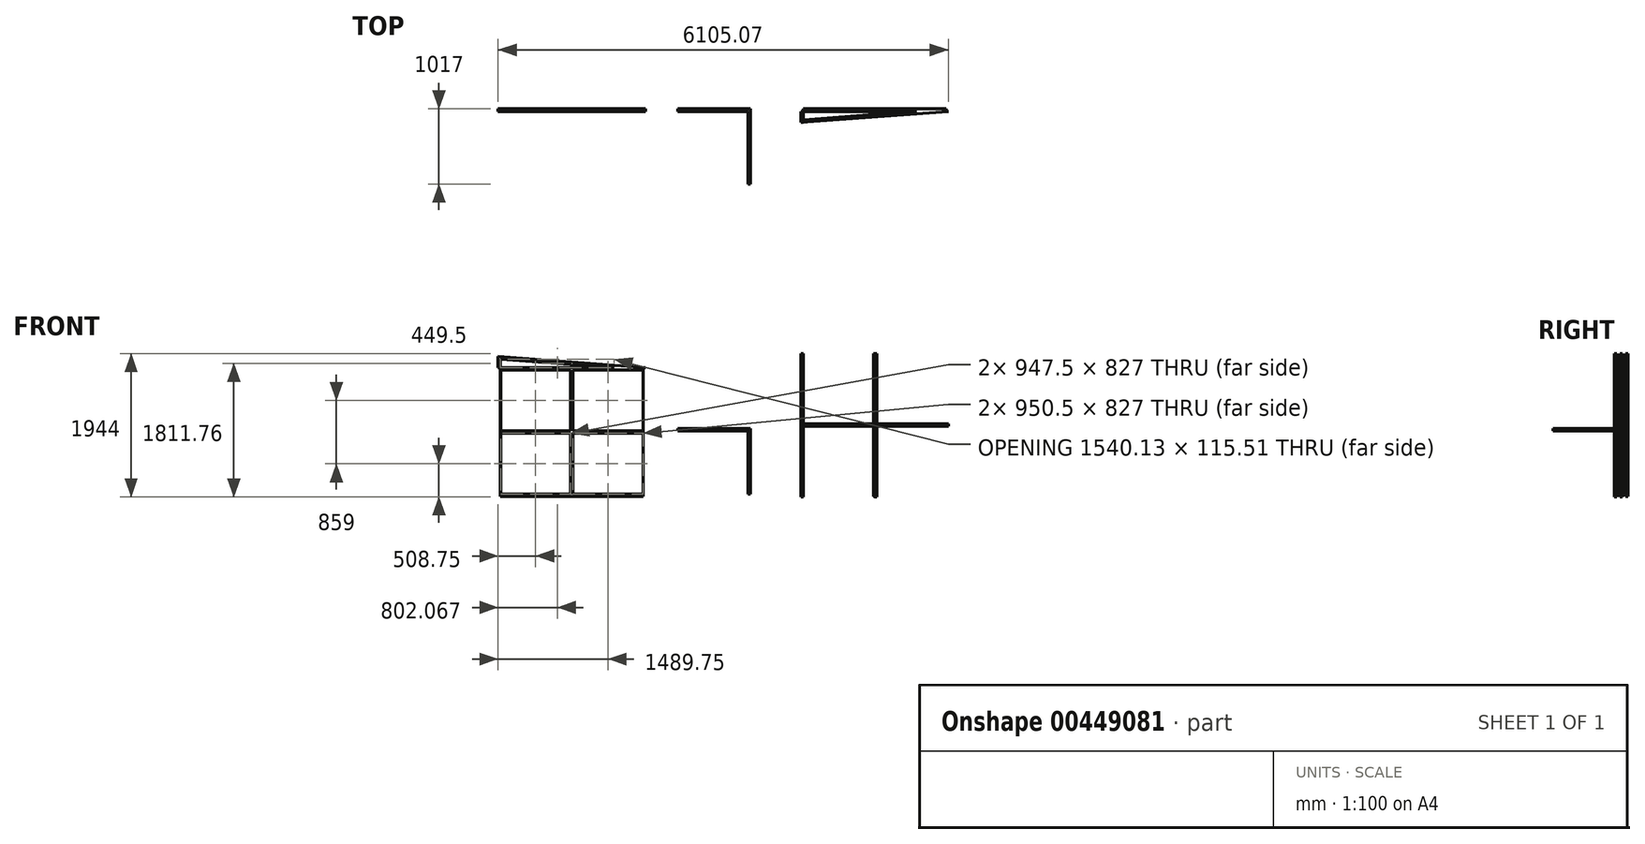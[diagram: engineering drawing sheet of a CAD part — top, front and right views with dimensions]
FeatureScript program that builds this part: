
annotation { "Feature Type Name" : "Feature", "Feature Type Description" : "" }
export const myFeature = defineFeature(function(context is Context, id is Id, definition is map)
    precondition{}
    {
        {
            var Q0;
            Q0=qCreatedBy(makeId("Front.planeOp"),FACE);
            var sketch = newSketch(context, id + "F0", { "sketchPlane" : qUnion([Q0])});
            skLineSegment(sketch, "E0.bottom", {"start": v(0, 0) * mm, "end": v(1936, 0) * mm});
            skLineSegment(sketch, "E0.top", {"start": v(1.2, 1750) * mm, "end": v(1540.14, 1750) * mm});
            skLineSegment(sketch, "E0.left", {"start": v(0, 0) * mm, "end": v(0, 1750) * mm});
            skLineSegment(sketch, "E0.right", {"start": v(1936, 0) * mm, "end": v(1936, 1750) * mm});
            skLineSegment(sketch, "E1.1", {"start": v(3, 32) * mm, "end": v(950.5, 32) * mm});
            skLineSegment(sketch, "E1.3", {"start": v(3, 1718) * mm, "end": v(1933, 1718) * mm});
            skLineSegment(sketch, "E2", {"start": v(966.5, 1718) * mm, "end": v(966.5, 32) * mm, "construction": true});
            skLineSegment(sketch, "E3", {"start": v(32, 875) * mm, "end": v(1904, 875) * mm, "construction": true});
            skLineSegment(sketch, "E4.left", {"start": v(950.5, 1718) * mm, "end": v(950.5, 32) * mm});
            skLineSegment(sketch, "E4.right", {"start": v(982.5, 1718) * mm, "end": v(982.5, 32) * mm});
            skLineSegment(sketch, "E5.bottom", {"start": v(1933, 891) * mm, "end": v(3, 891) * mm});
            skLineSegment(sketch, "E5.top", {"start": v(1933, 859) * mm, "end": v(3, 859) * mm});
            skLineSegment(sketch, "E6", {"start": v(1926.84, 875) * mm, "end": v(1904, 875) * mm, "construction": true});
            skLineSegment(sketch, "E7", {"start": v(966.5, 1718) * mm, "end": v(966.5, 1691.84) * mm, "construction": true});
            skLineSegment(sketch, "E8.0", {"start": v(3, 32) * mm, "end": v(3, 859) * mm});
            skLineSegment(sketch, "E9.0", {"start": v(1933, 0) * mm, "end": v(1933, 859) * mm});
            skPoint(sketch, "E10.orphan", {"position": v(1902.5, 1718) * mm});
            skPoint(sketch, "E11.orphan", {"position": v(30.5, 1718) * mm});
            skPoint(sketch, "E12.orphan", {"position": v(30.5, 32) * mm});
            skPoint(sketch, "E13.orphan", {"position": v(1902.5, 32) * mm});
            skLineSegment(sketch, "E14.bottom", {"start": v(3388.3, 34.62) * mm, "end": v(3356.3, 34.62) * mm});
            skLineSegment(sketch, "E14.top", {"start": v(3388.3, 925.62) * mm, "end": v(3356.3, 925.62) * mm});
            skLineSegment(sketch, "E14.left", {"start": v(3388.3, 34.62) * mm, "end": v(3388.3, 925.62) * mm});
            skLineSegment(sketch, "E14.right", {"start": v(3356.3, 34.62) * mm, "end": v(3356.3, 925.62) * mm});
            skLineSegment(sketch, "E15.bottom", {"start": v(3356.3, 925.62) * mm, "end": v(2404.3, 925.62) * mm});
            skLineSegment(sketch, "E15.top", {"start": v(3356.3, 893.62) * mm, "end": v(2404.3, 893.62) * mm});
            skLineSegment(sketch, "E15.left", {"start": v(3356.3, 925.62) * mm, "end": v(3356.3, 893.62) * mm});
            skLineSegment(sketch, "E15.right", {"start": v(2404.3, 925.62) * mm, "end": v(2404.3, 893.62) * mm});
            skLineSegment(sketch, "E16.bottom", {"start": v(5057.07, 1936) * mm, "end": v(5089.07, 1936) * mm});
            skLineSegment(sketch, "E16.top", {"start": v(5057.07, 0) * mm, "end": v(5089.07, 0) * mm});
            skLineSegment(sketch, "E16.left", {"start": v(5057.07, 1936) * mm, "end": v(5057.07, 0) * mm});
            skLineSegment(sketch, "E16.right", {"start": v(5089.07, 1936) * mm, "end": v(5089.07, 0) * mm});
            skLineSegment(sketch, "E17.bottom", {"start": v(4105.07, 984) * mm, "end": v(6041.07, 984) * mm});
            skLineSegment(sketch, "E17.top", {"start": v(4105.07, 952) * mm, "end": v(6041.07, 952) * mm});
            skLineSegment(sketch, "E17.left", {"start": v(4105.07, 984) * mm, "end": v(4105.07, 952) * mm});
            skLineSegment(sketch, "E17.right", {"start": v(6041.07, 984) * mm, "end": v(6041.07, 952) * mm});
            skLineSegment(sketch, "E18", {"start": v(0, 1750) * mm, "end": v(-32, 1750) * mm});
            skLineSegment(sketch, "E19", {"start": v(-32, 1750) * mm, "end": v(-32, 1900) * mm});
            skLineSegment(sketch, "E20", {"start": v(-32, 1900) * mm, "end": v(1968, 1750) * mm});
            skLineSegment(sketch, "E21", {"start": v(1968, 1750) * mm, "end": v(1936, 1750) * mm});
            skLineSegment(sketch, "E22.0", {"start": v(0, 1865.51) * mm, "end": v(1540.14, 1750) * mm});
            skLineSegment(sketch, "E22.1", {"start": v(0, 1750.87) * mm, "end": v(0, 1865.51) * mm});
            skPoint(sketch, "E23.orphan", {"position": v(1904, 891) * mm});
            skPoint(sketch, "E5.left.end.orphan", {"position": v(1904, 859) * mm});
            skLineSegment(sketch, "E24.trimOffspring", {"start": v(1933, 891) * mm, "end": v(1933, 1718) * mm});
            skLineSegment(sketch, "E25.trimOffspring", {"start": v(982.5, 32) * mm, "end": v(1933, 32) * mm});
            skLineSegment(sketch, "E26.trimOffspring", {"start": v(3, 891) * mm, "end": v(3, 1718) * mm});
            skLineSegment(sketch, "E27.bottom", {"start": v(0, 1750.87) * mm, "end": v(1.2, 1750.87) * mm});
            skLineSegment(sketch, "E27.right", {"start": v(1.2, 1750.87) * mm, "end": v(1.2, 1750) * mm});
            skSolve(sketch);
        }
        {
            var Q0;
            Q0=makeQuery(id+"F0.imprint","IMPRINT",FACE,{"disambiguationData":[TD([[makeQuery(id+"F0.imprint","IMPRINT",EDGE,{"derivedFrom":sQuery(id+"F0.wireOp",EDGE,"E14.bottom")}),-1.0]])]});
            var Q1;
            Q1=makeQuery(id+"F0.imprint","IMPRINT",FACE,{"disambiguationData":[TD([[makeQuery(id+"F0.imprint","IMPRINT",EDGE,{"derivedFrom":sQuery(id+"F0.wireOp",EDGE,"E15.bottom")}),1.0]])]});
            var Q2;
            {var subQ0=sQuery(id+"F0.wireOp",EDGE,"E16.bottom");Q2=makeQuery(id+"F0.imprint","IMPRINT",FACE,{"disambiguationData":[TD([[makeQuery(id+"F0.imprint","IMPRINT",EDGE,{"derivedFrom":subQ0}),-1.0]])]});}
            var Q3;
            {var subQ0=sQuery(id+"F0.wireOp",EDGE,"E16.top");Q3=makeQuery(id+"F0.imprint","IMPRINT",FACE,{"disambiguationData":[TD([[makeQuery(id+"F0.imprint","IMPRINT",EDGE,{"derivedFrom":subQ0}),1.0]])]});}
            var Q4;
            {var subQ5=sQuery(id+"F0.wireOp",EDGE,"E17.left");Q4=makeQuery(id+"F0.imprint","IMPRINT",FACE,{"disambiguationData":[TD([[makeQuery(id+"F0.imprint","IMPRINT",EDGE,{"derivedFrom":subQ5}),1.0]])]});}
            var Q5;
            {var subQ5=sQuery(id+"F0.wireOp",EDGE,"E17.right");Q5=makeQuery(id+"F0.imprint","IMPRINT",FACE,{"disambiguationData":[TD([[makeQuery(id+"F0.imprint","IMPRINT",EDGE,{"derivedFrom":subQ5}),-1.0]])]});}
            var Q6;
            Q6=makeQuery(id+"F0.imprint","IMPRINT",FACE,{"disambiguationData":[TD([[makeQuery(id+"F0.imprint","IMPRINT",EDGE,{"derivedFrom":sQuery(id+"F0.wireOp",EDGE,"E18")}),-1.0]])]});
            var Q7;
            {var subQ0=sQuery(id+"F0.wireOp",EDGE,"E17.bottom");var subQ1=sQuery(id+"F0.wireOp",EDGE,"E16.left");var subQ2=makeQuery(id+"F0.imprint","INTERSECT",VERTEX,{"derivedFrom":[subQ1,subQ0]});Q7=makeQuery(id+"F0.imprint","IMPRINT",FACE,{"disambiguationData":[TD([[makeQuery(id+"F0.imprint","IMPRINT",EDGE,{"disambiguationData":[TD([[subQ2,-1.0]])],"derivedFrom":subQ1}),1.0]])]});}
            var Q8;
            {var subQ3=sQuery(id+"F0.wireOp",EDGE,"E4.top");Q8=makeQuery(id+"F0.imprint","IMPRINT",FACE,{"disambiguationData":[TD([[makeQuery(id+"F0.imprint","IMPRINT",EDGE,{"derivedFrom":subQ3}),-1.0]])]});}
            var Q9;
            {var subQ0=sQuery(id+"F0.wireOp",EDGE,"E0.left");Q9=makeQuery(id+"F0.imprint","IMPRINT",FACE,{"disambiguationData":[TD([[makeQuery(id+"F0.imprint","IMPRINT",EDGE,{"derivedFrom":subQ0}),-1.0]])]});}
            var Q10;
            {var subQ4=sQuery(id+"F0.wireOp",EDGE,"E0.right");Q10=makeQuery(id+"F0.imprint","IMPRINT",FACE,{"disambiguationData":[TD([[makeQuery(id+"F0.imprint","IMPRINT",EDGE,{"derivedFrom":subQ4}),1.0]])]});}
            var Q11;
            {var subQ5=sQuery(id+"F0.wireOp",EDGE,"E5.right");Q11=makeQuery(id+"F0.imprint","IMPRINT",FACE,{"disambiguationData":[TD([[makeQuery(id+"F0.imprint","IMPRINT",EDGE,{"derivedFrom":subQ5}),1.0]])]});}
            var Q12;
            {var subQ0=sQuery(id+"F0.wireOp",EDGE,"E5.bottom");var subQ1=sQuery(id+"F0.wireOp",EDGE,"E4.left");var subQ2=makeQuery(id+"F0.imprint","INTERSECT",VERTEX,{"derivedFrom":[subQ1,subQ0]});Q12=makeQuery(id+"F0.imprint","IMPRINT",FACE,{"disambiguationData":[TD([[makeQuery(id+"F0.imprint","IMPRINT",EDGE,{"disambiguationData":[TD([[subQ2,-1.0]])],"derivedFrom":subQ1}),1.0]])]});}
            var Q13;
            {var subQ5=sQuery(id+"F0.wireOp",EDGE,"E5.left");Q13=makeQuery(id+"F0.imprint","IMPRINT",FACE,{"disambiguationData":[TD([[makeQuery(id+"F0.imprint","IMPRINT",EDGE,{"derivedFrom":subQ5}),-1.0]])]});}
            var Q14;
            {var subQ0=sQuery(id+"F0.wireOp",EDGE,"E4.top");Q14=makeQuery(id+"F0.imprint","IMPRINT",FACE,{"disambiguationData":[TD([[makeQuery(id+"F0.imprint","IMPRINT",EDGE,{"derivedFrom":subQ0}),1.0]])]});}
            var Q15;
            {var subQ3=sQuery(id+"F0.wireOp",EDGE,"E5.right");Q15=makeQuery(id+"F0.imprint","IMPRINT",FACE,{"disambiguationData":[TD([[makeQuery(id+"F0.imprint","IMPRINT",EDGE,{"derivedFrom":subQ3}),-1.0]])]});}
            var Q16;
            {var subQ3=sQuery(id+"F0.wireOp",EDGE,"E5.left");Q16=makeQuery(id+"F0.imprint","IMPRINT",FACE,{"disambiguationData":[TD([[makeQuery(id+"F0.imprint","IMPRINT",EDGE,{"derivedFrom":subQ3}),1.0]])]});}
            var Q17;
            {var subQ0=sQuery(id+"F0.wireOp",EDGE,"E4.left");var subQ1=sQuery(id+"F0.wireOp",EDGE,"E1.3");var subQ2=makeQuery(id+"F0.imprint","INTERSECT",VERTEX,{"derivedFrom":[subQ1,subQ0]});Q17=makeQuery(id+"F0.imprint","IMPRINT",FACE,{"disambiguationData":[TD([[makeQuery(id+"F0.imprint","IMPRINT",EDGE,{"disambiguationData":[TD([[subQ2,-1.0]])],"derivedFrom":subQ1}),-1.0]])]});}
            var Q18;
            {var subQ3=sQuery(id+"F0.wireOp",EDGE,"E8.0");var subQ6=sQuery(id+"F0.wireOp",EDGE,"E0.top");var subQ9=makeQuery(id+"F0.imprint","INTERSECT",VERTEX,{"derivedFrom":[subQ6,subQ3]});Q18=makeQuery(id+"F0.imprint","IMPRINT",FACE,{"disambiguationData":[TD([[makeQuery(id+"F0.imprint","IMPRINT",EDGE,{"disambiguationData":[TD([[subQ9,-1.0]])],"derivedFrom":subQ6}),-1.0]])]});}
            extrude(context, id + "F1", {"entities" : qUnion([Q0, Q1, Q2, Q3, Q4, Q5, Q6, Q7, Q8, Q9, Q10, Q11, Q12, Q13, Q14, Q15, Q16, Q17, Q18]), "depth" : 33 * mm});
        }
        {
            var Q0;
            Q0=makeQuery(id+"F1.opExtrude","CAP_FACE",FACE,{"disambiguationData":[OSD([sQuery(id+"F0.wireOp",EDGE,"E14.bottom"),sQuery(id+"F0.wireOp",EDGE,"E14.top"),sQuery(id+"F0.wireOp",EDGE,"E14.left"),sQuery(id+"F0.wireOp",EDGE,"E14.right"),sQuery(id+"F0.wireOp",EDGE,"E15.bottom"),sQuery(id+"F0.wireOp",EDGE,"E15.top"),sQuery(id+"F0.wireOp",EDGE,"E15.right")])],"isStart":false});
            var sketch = newSketch(context, id + "F2", { "sketchPlane" : qUnion([Q0])});
            skLineSegment(sketch, "E28.bottom", {"start": v(3356.3, 893.62) * mm, "end": v(3388.3, 893.62) * mm});
            skLineSegment(sketch, "E28.top", {"start": v(3356.3, 925.62) * mm, "end": v(3388.3, 925.62) * mm});
            skLineSegment(sketch, "E28.left", {"start": v(3356.3, 893.62) * mm, "end": v(3356.3, 925.62) * mm});
            skLineSegment(sketch, "E28.right", {"start": v(3388.3, 893.62) * mm, "end": v(3388.3, 925.62) * mm});
            skSolve(sketch);
        }
        {
            var Q0;
            Q0=makeQuery(id+"F2.imprint","IMPRINT",FACE,{"disambiguationData":[TD([[makeQuery(id+"F2.imprint","IMPRINT",EDGE,{"derivedFrom":sQuery(id+"F2.wireOp",EDGE,"E28.bottom")}),1.0]])]});
            extrude(context, id + "F3", {"entities" : qUnion([Q0]), "operationType" : NewBodyOperationType.ADD, "depth" : 984 * mm});
        }
        {
            var Q0;
            {var subQ0=sQuery(id+"F0.wireOp",EDGE,"E17.top");Q0=makeQuery(id+"F1.opExtrude","SWEPT_FACE",FACE,{"disambiguationData":[OSD([subQ0]),TDD([makeQuery(id+"F0.imprint","IMPRINT",EDGE,{"disambiguationData":[TD([[makeQuery(id+"F0.imprint","INTERSECT",VERTEX,{"derivedFrom":[subQ0,sQuery(id+"F0.wireOp",EDGE,"E17.left")]}),-1.0]])],"derivedFrom":subQ0})])]});}
            var sketch = newSketch(context, id + "F4", { "sketchPlane" : qUnion([Q0])});
            skLineSegment(sketch, "E29", {"start": v(4105.07, 33) * mm, "end": v(4073.07, 33) * mm});
            skLineSegment(sketch, "E30", {"start": v(4073.07, 33) * mm, "end": v(4073.07, 183) * mm});
            skLineSegment(sketch, "E31", {"start": v(4073.07, 183) * mm, "end": v(6073.07, 33) * mm});
            skLineSegment(sketch, "E32", {"start": v(6073.07, 33) * mm, "end": v(6041.07, 33) * mm});
            skLineSegment(sketch, "E33", {"start": v(6041.07, 33) * mm, "end": v(4107.33, 33) * mm});
            skLineSegment(sketch, "E34.0", {"start": v(4105.07, 148.51) * mm, "end": v(5645.2, 33) * mm});
            skLineSegment(sketch, "E34.1", {"start": v(4105.07, 35.02) * mm, "end": v(4105.07, 148.51) * mm});
            skLineSegment(sketch, "E35.bottom", {"start": v(4105.07, 33) * mm, "end": v(4107.33, 33) * mm});
            skLineSegment(sketch, "E35.top", {"start": v(4105.07, 35.02) * mm, "end": v(4107.33, 35.02) * mm});
            skLineSegment(sketch, "E35.right", {"start": v(4107.33, 33) * mm, "end": v(4107.33, 35.02) * mm});
            skPoint(sketch, "E36.orphan", {"position": v(4105.07, 33) * mm});
            skSolve(sketch);
        }
        {
            var Q0;
            Q0=makeQuery(id+"F4.imprint","IMPRINT",FACE,{"disambiguationData":[TD([[makeQuery(id+"F4.imprint","IMPRINT",EDGE,{"derivedFrom":sQuery(id+"F4.wireOp",EDGE,"E29")}),-1.0]])]});
            extrude(context, id + "F5", {"entities" : qUnion([Q0]), "operationType" : NewBodyOperationType.ADD, "oppositeDirection" : true, "depth" : 32 * mm});
        }
        {
            var Q0;
            {var subQ0=sQuery(id+"F0.wireOp",EDGE,"E17.top");Q0=makeQuery(id+"F5.boolean.opBoolean","MERGE",FACE,{"derivedFrom":[makeQuery(id+"F1.opExtrude","SWEPT_FACE",FACE,{"disambiguationData":[OSD([subQ0]),TDD([makeQuery(id+"F0.imprint","IMPRINT",EDGE,{"disambiguationData":[TD([[makeQuery(id+"F0.imprint","INTERSECT",VERTEX,{"derivedFrom":[subQ0,sQuery(id+"F0.wireOp",EDGE,"E17.left")]}),-1.0]])],"derivedFrom":subQ0})])]}),makeQuery(id+"F1.opExtrude","SWEPT_FACE",FACE,{"disambiguationData":[OSD([subQ0]),TDD([makeQuery(id+"F0.imprint","IMPRINT",EDGE,{"disambiguationData":[TD([[makeQuery(id+"F0.imprint","INTERSECT",VERTEX,{"derivedFrom":[subQ0,sQuery(id+"F0.wireOp",EDGE,"E17.right")]}),1.0]])],"derivedFrom":subQ0})])]}),makeQuery(id+"F5.opExtrude","CAP_FACE",FACE,{"disambiguationData":[OSD([sQuery(id+"F4.wireOp",EDGE,"E29"),sQuery(id+"F4.wireOp",EDGE,"E30"),sQuery(id+"F4.wireOp",EDGE,"E31"),sQuery(id+"F4.wireOp",EDGE,"E32"),sQuery(id+"F4.wireOp",EDGE,"E33"),sQuery(id+"F4.wireOp",EDGE,"E34.0"),sQuery(id+"F4.wireOp",EDGE,"E34.1"),sQuery(id+"F4.wireOp",EDGE,"E35.bottom"),sQuery(id+"F4.wireOp",EDGE,"E35.top"),sQuery(id+"F4.wireOp",EDGE,"E35.right")])],"isStart":true})]});}
            var sketch = newSketch(context, id + "F6", { "sketchPlane" : qUnion([Q0])});
            skLineSegment(sketch, "E37.bottom", {"start": v(4105.07, 148.51) * mm, "end": v(4073.07, 148.51) * mm});
            skLineSegment(sketch, "E37.top", {"start": v(4105.07, 180.51) * mm, "end": v(4073.07, 180.51) * mm});
            skLineSegment(sketch, "E37.left", {"start": v(4105.07, 148.51) * mm, "end": v(4105.07, 180.51) * mm});
            skLineSegment(sketch, "E37.right", {"start": v(4073.07, 148.51) * mm, "end": v(4073.07, 180.51) * mm});
            skLineSegment(sketch, "E38", {"start": v(5073.37, 75.89) * mm, "end": v(5073.37, 107.89) * mm});
            skLineSegment(sketch, "E39", {"start": v(5073.37, 107.89) * mm, "end": v(5105.28, 105.5) * mm});
            skLineSegment(sketch, "E40", {"start": v(5105.28, 105.5) * mm, "end": v(5105.28, 73.5) * mm});
            skLineSegment(sketch, "E41", {"start": v(5105.28, 73.5) * mm, "end": v(5073.37, 75.89) * mm});
            skSolve(sketch);
        }
        {
            var Q0;
            Q0 = qSketchRegion(id + "F6", true);
            extrude(context, id + "F7", {"entities" : qUnion([Q0]), "operationType" : NewBodyOperationType.ADD, "depth" : 956 * mm});
        }
        {
            var Q0;
            Q0 = qSketchRegion(id + "F6", true);
            extrude(context, id + "F8", {"entities" : qUnion([Q0]), "operationType" : NewBodyOperationType.ADD, "oppositeDirection" : true, "depth" : (956 + 32) * mm});
        }
    });
